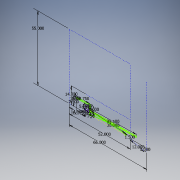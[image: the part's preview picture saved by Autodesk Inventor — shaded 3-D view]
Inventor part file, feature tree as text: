
AUTODESK INVENTOR PART (.ipt)
format: ipt  version: 2017 SP1 (Build 210196100, 196)  size: 122,880 bytes
history: native  units: in
note: dims shown in document units (in); Inventor stores cm internally (conversion verified against a paired STEP export)
features: sketch x1
ambient origin geometry x8: Origin, YZ Plane, XZ Plane, XY Plane, X Axis, Y Axis, Z Axis, Center Point
feature tree (1):
  sketch  "Sketch1"  dims[d0=5.0in d1=2.0in d3=1.0in d4=7.5in d5=7.5in d7=10.75in d10=1.25in d11=3.25in d13=39.5in d16=14.0in d21=8.0in d35=0.75in d36=1.5in d37=30.0in d38=14.0in d39=52.0in d40=66.0in d41=3.0in d42=12.0in d43=55.0in d44=0.625in]
